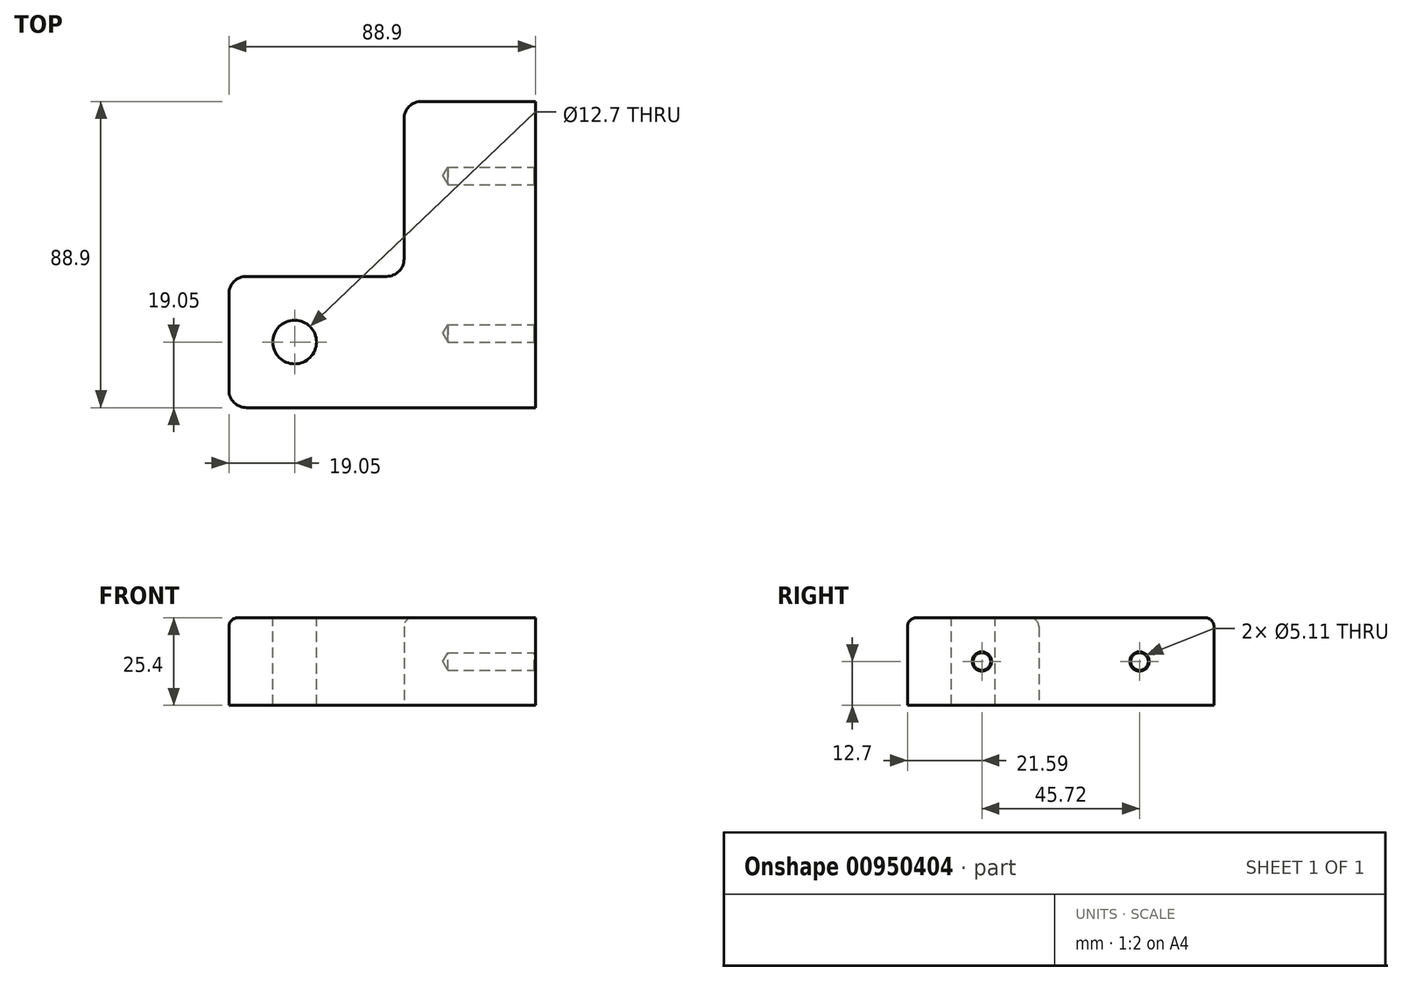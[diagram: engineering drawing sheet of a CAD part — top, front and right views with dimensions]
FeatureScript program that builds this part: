
annotation { "Feature Type Name" : "Feature", "Feature Type Description" : "" }
export const myFeature = defineFeature(function(context is Context, id is Id, definition is map)
    precondition{}
    {
        {
            var Q0;
            Q0=qCreatedBy(makeId("Top.planeOp"),FACE);
            var sketch = newSketch(context, id + "F0", { "sketchPlane" : qUnion([Q0])});
            skLineSegment(sketch, "E0", {"start": v(0, 0) * mm, "end": v(0, 50.8) * mm});
            skLineSegment(sketch, "E1", {"start": v(0, 50.8) * mm, "end": v(38.1, 50.8) * mm});
            skLineSegment(sketch, "E2", {"start": v(38.1, 50.8) * mm, "end": v(38.1, -38.1) * mm});
            skLineSegment(sketch, "E3", {"start": v(38.1, -38.1) * mm, "end": v(-50.8, -38.1) * mm});
            skLineSegment(sketch, "E4", {"start": v(-50.8, -38.1) * mm, "end": v(-50.8, 0) * mm});
            skLineSegment(sketch, "E5", {"start": v(-50.8, 0) * mm, "end": v(0, 0) * mm});
            skSolve(sketch);
        }
        {
            var Q0;
            Q0=makeQuery(id+"F0.imprint","IMPRINT",FACE,{"disambiguationData":[TD([[makeQuery(id+"F0.imprint","IMPRINT",EDGE,{"derivedFrom":sQuery(id+"F0.wireOp",EDGE,"E0")}),-1.0]])]});
            extrude(context, id + "F1", {"entities" : qUnion([Q0]), "depth" : 25.4 * mm, "offsetDistance" : 25.4 * mm});
        }
        {
            var Q0;
            Q0=makeQuery(id+"F1.opExtrude","CAP_FACE",FACE,{"disambiguationData":[OSD([sQuery(id+"F0.wireOp",EDGE,"E0"),sQuery(id+"F0.wireOp",EDGE,"E1"),sQuery(id+"F0.wireOp",EDGE,"E2"),sQuery(id+"F0.wireOp",EDGE,"E3"),sQuery(id+"F0.wireOp",EDGE,"E4"),sQuery(id+"F0.wireOp",EDGE,"E5")])],"isStart":false});
            var sketch = newSketch(context, id + "F2", { "sketchPlane" : qUnion([Q0])});
            skCircle(sketch, "E6", {"center": v(-31.75, -19.05) * mm, "radius": 6.35 * mm});
            skSolve(sketch);
        }
        {
            var Q0;
            Q0=makeQuery(id+"F2.imprint","IMPRINT",FACE,{"disambiguationData":[TD([[makeQuery(id+"F2.imprint","IMPRINT",EDGE,{"derivedFrom":sQuery(id+"F2.wireOp",EDGE,"E6")}),1.0]])]});
            var Q1;
            Q1=sQuery(id+"F2.wireOp",EDGE,"E6");
            extrude(context, id + "F3", {"entities" : qUnion([Q0]), "operationType" : NewBodyOperationType.REMOVE, "surfaceEntities" : qUnion([Q1]), "endBound" : BoundingType.UP_TO_NEXT, "oppositeDirection" : true, "depth" : 25.4 * mm, "offsetDistance" : 25.4 * mm});
        }
        {
            var Q0;
            Q0=makeQuery(id+"F1.opExtrude","SWEPT_EDGE",EDGE,{"disambiguationData":[OSD([sQuery(id+"F0.wireOp",EDGE,"E3"),sQuery(id+"F0.wireOp",EDGE,"E4")])]});
            var Q1;
            Q1=makeQuery(id+"F1.opExtrude","SWEPT_EDGE",EDGE,{"disambiguationData":[OSD([sQuery(id+"F0.wireOp",EDGE,"E4"),sQuery(id+"F0.wireOp",EDGE,"E5")])]});
            var Q2;
            Q2=makeQuery(id+"F1.opExtrude","SWEPT_EDGE",EDGE,{"disambiguationData":[OSD([sQuery(id+"F0.wireOp",EDGE,"E0"),sQuery(id+"F0.wireOp",EDGE,"E5")])]});
            var Q3;
            Q3=makeQuery(id+"F1.opExtrude","SWEPT_EDGE",EDGE,{"disambiguationData":[OSD([sQuery(id+"F0.wireOp",EDGE,"E0"),sQuery(id+"F0.wireOp",EDGE,"E1")])]});
            fillet(context, id + "F4", {"entities" : qUnion([Q0, Q1, Q2, Q3]), "radius" : 5.08 * mm, "tangentPropagation" : true, "allowEdgeOverflow" : false});
        }
        {
            var Q0;
            Q0=makeQuery(id+"F1.opExtrude","CAP_EDGE",EDGE,{"disambiguationData":[OSD([sQuery(id+"F0.wireOp",EDGE,"E3")])],"isStart":false});
            fillet(context, id + "F5", {"entities" : qUnion([Q0]), "radius" : 2.54 * mm, "tangentPropagation" : true, "allowEdgeOverflow" : false});
        }
        {
            var Q0;
            Q0=makeQuery(id+"F1.opExtrude","SWEPT_FACE",FACE,{"disambiguationData":[OSD([sQuery(id+"F0.wireOp",EDGE,"E2")])]});
            var sketch = newSketch(context, id + "F6", { "sketchPlane" : qUnion([Q0])});
            skPoint(sketch, "E7", {"position": v(-16.51, 12.7) * mm});
            skPoint(sketch, "E8", {"position": v(29.2, 12.7) * mm});
            skSolve(sketch);
        }
        {
            var Q0;
            Q0=sQuery(id+"F6.wireOp",VERTEX,"E8");
            var Q1;
            Q1=sQuery(id+"F6.wireOp",VERTEX,"E7");
            var Q2;
            Q2=makeQuery(id+"F1.opExtrude","SWEPT_BODY",BODY,{"disambiguationData":[OSD([sQuery(id+"F0.wireOp",EDGE,"E0"),sQuery(id+"F0.wireOp",EDGE,"E1"),sQuery(id+"F0.wireOp",EDGE,"E2"),sQuery(id+"F0.wireOp",EDGE,"E3"),sQuery(id+"F0.wireOp",EDGE,"E4"),sQuery(id+"F0.wireOp",EDGE,"E5")])]});
            hole(context, id + "F7", {"style" : HoleStyle.C_SINK, "endStyle" : HoleEndStyle.BLIND, "holeDiameter" : 5.1 * mm, "cSinkDiameter" : 5.6 * mm, "cSinkAngle" : 82 * degree, "majorDiameter" : 6.35 * mm, "holeDepth" : 25.4 * mm, "isTappedThrough" : true, "tappedDepth" : 21.59 * mm, "tapClearance" : 3, "locations" : qUnion([Q0, Q1]), "scope" : qUnion([Q2])});
        }
    });
